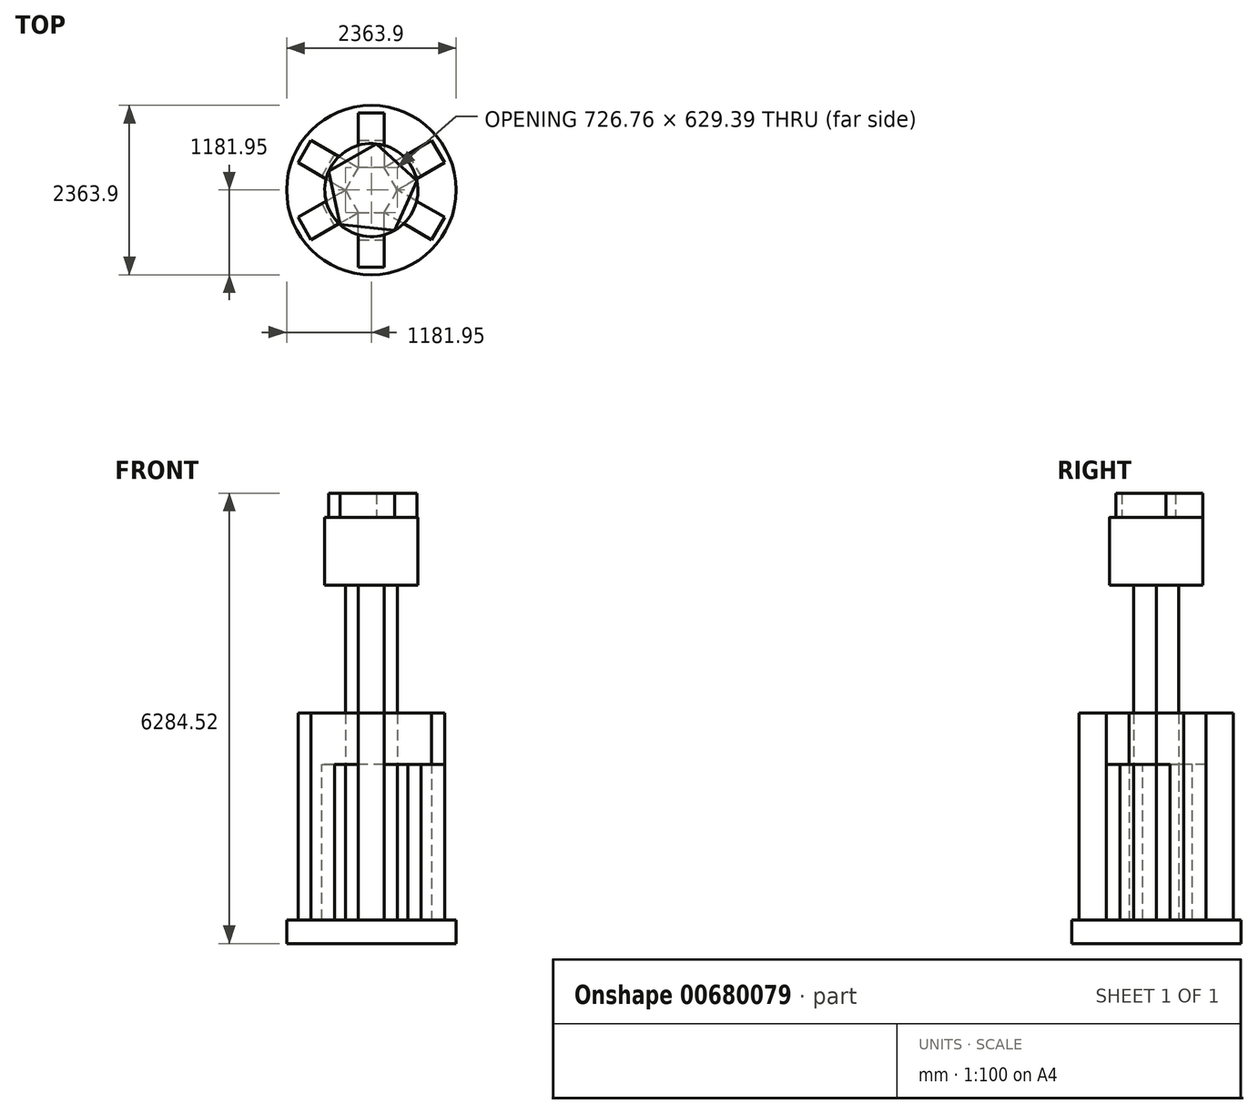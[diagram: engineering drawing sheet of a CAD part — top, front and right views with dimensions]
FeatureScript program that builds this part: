
annotation { "Feature Type Name" : "Feature", "Feature Type Description" : "" }
export const myFeature = defineFeature(function(context is Context, id is Id, definition is map)
    precondition{}
    {
        {
            var Q0;
            Q0=qCreatedBy(makeId("Top.planeOp"),FACE);
            var sketch = newSketch(context, id + "F0", { "sketchPlane" : qUnion([Q0])});
            skCircle(sketch, "E0.cCircle", {"center": v(0, 0) * mm, "radius": 363.38 * mm, "construction": true});
            skLineSegment(sketch, "E0.0", {"start": v(363.38, 0) * mm, "end": v(181.69, -314.7) * mm});
            skLineSegment(sketch, "E0.1", {"start": v(181.69, -314.7) * mm, "end": v(-181.69, -314.7) * mm});
            skLineSegment(sketch, "E0.2", {"start": v(-181.69, -314.7) * mm, "end": v(-363.38, 0) * mm});
            skLineSegment(sketch, "E0.3", {"start": v(-363.38, 0) * mm, "end": v(-181.69, 314.7) * mm});
            skLineSegment(sketch, "E0.4", {"start": v(-181.69, 314.7) * mm, "end": v(181.69, 314.7) * mm});
            skLineSegment(sketch, "E0.5", {"start": v(181.69, 314.7) * mm, "end": v(363.38, 0) * mm});
            skSolve(sketch);
        }
        {
            var Q0;
            Q0=makeQuery(id+"F0.imprint","IMPRINT",FACE,{"disambiguationData":[TD([[makeQuery(id+"F0.imprint","IMPRINT",EDGE,{"derivedFrom":sQuery(id+"F0.wireOp",EDGE,"E0.0")}),-1.0]])]});
            extrude(context, id + "F1", {"entities" : qUnion([Q0]), "depth" : 5000 * mm, "offsetDistance" : 25.4 * mm});
        }
        {
            var Q0;
            Q0=makeQuery(id+"F1.opExtrude","CAP_FACE",FACE,{"disambiguationData":[OSD([sQuery(id+"F0.wireOp",EDGE,"E0.0"),sQuery(id+"F0.wireOp",EDGE,"E0.1"),sQuery(id+"F0.wireOp",EDGE,"E0.2"),sQuery(id+"F0.wireOp",EDGE,"E0.3"),sQuery(id+"F0.wireOp",EDGE,"E0.4"),sQuery(id+"F0.wireOp",EDGE,"E0.5")])],"isStart":false});
            var sketch = newSketch(context, id + "F2", { "sketchPlane" : qUnion([Q0])});
            skCircle(sketch, "E1", {"center": v(0, 0) * mm, "radius": 650.1 * mm});
            skSolve(sketch);
        }
        {
            var Q0;
            Q0 = qSketchRegion(id + "F2", true);
            extrude(context, id + "F3", {"entities" : qUnion([Q0]), "operationType" : NewBodyOperationType.ADD, "depth" : 199.2 * mm, "offsetDistance" : 25.4 * mm});
        }
        {
            var Q0;
            Q0=makeQuery(id+"F1.opExtrude","SWEPT_FACE",FACE,{"disambiguationData":[OSD([sQuery(id+"F0.wireOp",EDGE,"E0.0")])]});
            var sketch = newSketch(context, id + "F4", { "sketchPlane" : qUnion([Q0])});
            skLineSegment(sketch, "E2.bottom", {"start": v(181.69, 3215.1) * mm, "end": v(-181.69, 3215.1) * mm});
            skLineSegment(sketch, "E2.top", {"start": v(181.69, 2500) * mm, "end": v(-181.69, 2500) * mm});
            skLineSegment(sketch, "E2.left", {"start": v(181.69, 3215.1) * mm, "end": v(181.69, 2500) * mm});
            skLineSegment(sketch, "E2.right", {"start": v(-181.69, 3215.1) * mm, "end": v(-181.69, 2500) * mm});
            skSolve(sketch);
        }
        {
            var Q0;
            Q0 = qSketchRegion(id + "F4", true);
            extrude(context, id + "F5", {"entities" : qUnion([Q0]), "operationType" : NewBodyOperationType.ADD, "depth" : 762 * mm, "offsetDistance" : 25.4 * mm});
        }
        {
            var Q0;
            Q0=makeQuery(id+"F1.opExtrude","SWEPT_FACE",FACE,{"disambiguationData":[OSD([sQuery(id+"F0.wireOp",EDGE,"E0.5")])]});
            var sketch = newSketch(context, id + "F6", { "sketchPlane" : qUnion([Q0])});
            skLineSegment(sketch, "E3.bottom", {"start": v(-181.69, 3215.1) * mm, "end": v(181.69, 3215.1) * mm});
            skLineSegment(sketch, "E3.top", {"start": v(-181.69, 2500) * mm, "end": v(181.69, 2500) * mm});
            skLineSegment(sketch, "E3.left", {"start": v(-181.69, 3215.1) * mm, "end": v(-181.69, 2500) * mm});
            skLineSegment(sketch, "E3.right", {"start": v(181.69, 3215.1) * mm, "end": v(181.69, 2500) * mm});
            skSolve(sketch);
        }
        {
            var Q0;
            Q0=makeQuery(id+"F6.imprint","IMPRINT",FACE,{"disambiguationData":[TD([[makeQuery(id+"F6.imprint","IMPRINT",EDGE,{"derivedFrom":sQuery(id+"F6.wireOp",EDGE,"E3.bottom")}),-1.0]])]});
            extrude(context, id + "F7", {"entities" : qUnion([Q0]), "operationType" : NewBodyOperationType.ADD, "depth" : 762 * mm, "offsetDistance" : 25.4 * mm});
        }
        {
            var Q0;
            Q0=makeQuery(id+"F1.opExtrude","SWEPT_FACE",FACE,{"disambiguationData":[OSD([sQuery(id+"F0.wireOp",EDGE,"E0.4")])]});
            var sketch = newSketch(context, id + "F8", { "sketchPlane" : qUnion([Q0])});
            skLineSegment(sketch, "E4.bottom", {"start": v(-181.69, 3215.1) * mm, "end": v(181.69, 3215.1) * mm});
            skLineSegment(sketch, "E4.top", {"start": v(-181.69, 2500) * mm, "end": v(181.69, 2500) * mm});
            skLineSegment(sketch, "E4.left", {"start": v(-181.69, 3215.1) * mm, "end": v(-181.69, 2500) * mm});
            skLineSegment(sketch, "E4.right", {"start": v(181.69, 3215.1) * mm, "end": v(181.69, 2500) * mm});
            skSolve(sketch);
        }
        {
            var Q0;
            Q0 = qSketchRegion(id + "F8", true);
            extrude(context, id + "F9", {"entities" : qUnion([Q0]), "operationType" : NewBodyOperationType.ADD, "depth" : 762 * mm, "offsetDistance" : 25.4 * mm});
        }
        {
            var Q0;
            Q0=makeQuery(id+"F1.opExtrude","SWEPT_FACE",FACE,{"disambiguationData":[OSD([sQuery(id+"F0.wireOp",EDGE,"E0.3")])]});
            var sketch = newSketch(context, id + "F10", { "sketchPlane" : qUnion([Q0])});
            skLineSegment(sketch, "E5.bottom", {"start": v(-181.69, 3215.1) * mm, "end": v(181.69, 3215.1) * mm});
            skLineSegment(sketch, "E5.top", {"start": v(-181.69, 2500) * mm, "end": v(181.69, 2500) * mm});
            skLineSegment(sketch, "E5.left", {"start": v(-181.69, 3215.1) * mm, "end": v(-181.69, 2500) * mm});
            skLineSegment(sketch, "E5.right", {"start": v(181.69, 3215.1) * mm, "end": v(181.69, 2500) * mm});
            skSolve(sketch);
        }
        {
            var Q0;
            Q0 = qSketchRegion(id + "F10", true);
            extrude(context, id + "F11", {"entities" : qUnion([Q0]), "operationType" : NewBodyOperationType.ADD, "depth" : 762 * mm, "offsetDistance" : 25.4 * mm});
        }
        {
            var Q0;
            Q0=makeQuery(id+"F1.opExtrude","SWEPT_FACE",FACE,{"disambiguationData":[OSD([sQuery(id+"F0.wireOp",EDGE,"E0.1")])]});
            var sketch = newSketch(context, id + "F12", { "sketchPlane" : qUnion([Q0])});
            skLineSegment(sketch, "E6.bottom", {"start": v(181.69, 3215.1) * mm, "end": v(-181.69, 3215.1) * mm});
            skLineSegment(sketch, "E6.top", {"start": v(181.69, 2500) * mm, "end": v(-181.69, 2500) * mm});
            skLineSegment(sketch, "E6.left", {"start": v(181.69, 3215.1) * mm, "end": v(181.69, 2500) * mm});
            skLineSegment(sketch, "E6.right", {"start": v(-181.69, 3215.1) * mm, "end": v(-181.69, 2500) * mm});
            skSolve(sketch);
        }
        {
            var Q0;
            Q0=makeQuery(id+"F12.imprint","IMPRINT",FACE,{"disambiguationData":[TD([[makeQuery(id+"F12.imprint","IMPRINT",EDGE,{"derivedFrom":sQuery(id+"F12.wireOp",EDGE,"E6.bottom")}),1.0]])]});
            extrude(context, id + "F13", {"entities" : qUnion([Q0]), "operationType" : NewBodyOperationType.ADD, "depth" : 762 * mm, "offsetDistance" : 25.4 * mm});
        }
        {
            var Q0;
            Q0=makeQuery(id+"F1.opExtrude","SWEPT_FACE",FACE,{"disambiguationData":[OSD([sQuery(id+"F0.wireOp",EDGE,"E0.2")])]});
            var sketch = newSketch(context, id + "F14", { "sketchPlane" : qUnion([Q0])});
            skLineSegment(sketch, "E7.bottom", {"start": v(-181.69, 3215.1) * mm, "end": v(181.69, 3215.1) * mm});
            skLineSegment(sketch, "E7.top", {"start": v(-181.69, 2500) * mm, "end": v(181.69, 2500) * mm});
            skLineSegment(sketch, "E7.left", {"start": v(-181.69, 3215.1) * mm, "end": v(-181.69, 2500) * mm});
            skLineSegment(sketch, "E7.right", {"start": v(181.69, 3215.1) * mm, "end": v(181.69, 2500) * mm});
            skSolve(sketch);
        }
        {
            var Q0;
            Q0=makeQuery(id+"F14.imprint","IMPRINT",FACE,{"disambiguationData":[TD([[makeQuery(id+"F14.imprint","IMPRINT",EDGE,{"derivedFrom":sQuery(id+"F14.wireOp",EDGE,"E7.bottom")}),-1.0]])]});
            extrude(context, id + "F15", {"entities" : qUnion([Q0]), "operationType" : NewBodyOperationType.ADD, "depth" : 762 * mm, "offsetDistance" : 25.4 * mm});
        }
        {
            var Q0;
            Q0=makeQuery(id+"F1.opExtrude","CAP_FACE",FACE,{"disambiguationData":[OSD([sQuery(id+"F0.wireOp",EDGE,"E0.0"),sQuery(id+"F0.wireOp",EDGE,"E0.1"),sQuery(id+"F0.wireOp",EDGE,"E0.2"),sQuery(id+"F0.wireOp",EDGE,"E0.3"),sQuery(id+"F0.wireOp",EDGE,"E0.4"),sQuery(id+"F0.wireOp",EDGE,"E0.5")])],"isStart":true});
            var sketch = newSketch(context, id + "F16", { "sketchPlane" : qUnion([Q0])});
            skCircle(sketch, "E8", {"center": v(0, 0) * mm, "radius": 1181.95 * mm});
            skSolve(sketch);
        }
        {
            var Q0;
            Q0 = qSketchRegion(id + "F16", true);
            extrude(context, id + "F17", {"entities" : qUnion([Q0]), "operationType" : NewBodyOperationType.ADD, "oppositeDirection" : true, "depth" : 326.88 * mm, "offsetDistance" : 25.4 * mm});
        }
        {
            var Q0;
            Q0=makeQuery(id+"F9.opExtrude","SWEPT_FACE",FACE,{"disambiguationData":[OSD([sQuery(id+"F8.wireOp",EDGE,"E4.top")])]});
            var sketch = newSketch(context, id + "F18", { "sketchPlane" : qUnion([Q0])});
            skLineSegment(sketch, "E9", {"start": v(181.69, -695.7) * mm, "end": v(-181.69, -695.7) * mm});
            skSolve(sketch);
        }
        {
            var Q0;
            {var subQ0=sQuery(id+"F18.wireOp",EDGE,"E9");Q0=makeQuery(id+"F18.imprint","IMPRINT",FACE,{"disambiguationData":[TD([[makeQuery(id+"F18.imprint","IMPRINT",EDGE,{"derivedFrom":subQ0}),1.0]])]});}
            extrude(context, id + "F19", {"entities" : qUnion([Q0]), "operationType" : NewBodyOperationType.ADD, "depth" : 1809.93 * mm, "offsetDistance" : 25.4 * mm});
        }
        {
            var Q0;
            Q0=makeQuery(id+"F7.opExtrude","SWEPT_FACE",FACE,{"disambiguationData":[OSD([sQuery(id+"F6.wireOp",EDGE,"E3.top")])]});
            var sketch = newSketch(context, id + "F20", { "sketchPlane" : qUnion([Q0])});
            skLineSegment(sketch, "E10", {"start": v(693.34, -190.5) * mm, "end": v(511.65, -505.2) * mm});
            skSolve(sketch);
        }
        {
            var Q0;
            Q0=makeQuery(id+"F5.opExtrude","SWEPT_FACE",FACE,{"disambiguationData":[OSD([sQuery(id+"F4.wireOp",EDGE,"E2.top")])]});
            var sketch = newSketch(context, id + "F21", { "sketchPlane" : qUnion([Q0])});
            skLineSegment(sketch, "E11", {"start": v(511.65, 505.2) * mm, "end": v(693.34, 190.5) * mm});
            skLineSegment(sketch, "E12", {"start": v(693.34, 190.5) * mm, "end": v(511.65, 505.2) * mm});
            skSolve(sketch);
        }
        {
            var Q0;
            Q0=makeQuery(id+"F13.opExtrude","SWEPT_FACE",FACE,{"disambiguationData":[OSD([sQuery(id+"F12.wireOp",EDGE,"E6.top")])]});
            var sketch = newSketch(context, id + "F22", { "sketchPlane" : qUnion([Q0])});
            skLineSegment(sketch, "E13", {"start": v(181.69, 695.7) * mm, "end": v(-181.69, 695.7) * mm});
            skSolve(sketch);
        }
        {
            var Q0;
            Q0=makeQuery(id+"F15.opExtrude","SWEPT_FACE",FACE,{"disambiguationData":[OSD([sQuery(id+"F14.wireOp",EDGE,"E7.top")])]});
            var sketch = newSketch(context, id + "F23", { "sketchPlane" : qUnion([Q0])});
            skLineSegment(sketch, "E14", {"start": v(-511.65, 505.2) * mm, "end": v(-693.34, 190.5) * mm});
            skSolve(sketch);
        }
        {
            var Q0;
            {var subQ0=sQuery(id+"F20.wireOp",EDGE,"E10");Q0=makeQuery(id+"F20.imprint","IMPRINT",FACE,{"disambiguationData":[TD([[makeQuery(id+"F20.imprint","IMPRINT",EDGE,{"derivedFrom":subQ0}),1.0]])]});}
            var Q1;
            {var subQ0=sQuery(id+"F23.wireOp",EDGE,"E14");Q1=makeQuery(id+"F23.imprint","IMPRINT",FACE,{"disambiguationData":[TD([[makeQuery(id+"F23.imprint","IMPRINT",EDGE,{"derivedFrom":subQ0}),-1.0]])]});}
            var Q2;
            {var subQ0=sQuery(id+"F22.wireOp",EDGE,"E13");Q2=makeQuery(id+"F22.imprint","IMPRINT",FACE,{"disambiguationData":[TD([[makeQuery(id+"F22.imprint","IMPRINT",EDGE,{"derivedFrom":subQ0}),-1.0]])]});}
            var Q3;
            {var subQ0=sQuery(id+"F21.wireOp",EDGE,"E12");Q3=makeQuery(id+"F21.imprint","IMPRINT",FACE,{"disambiguationData":[TD([[makeQuery(id+"F21.imprint","IMPRINT",EDGE,{"derivedFrom":subQ0}),-1.0]])]});}
            extrude(context, id + "F24", {"entities" : qUnion([Q0, Q1, Q2, Q3]), "operationType" : NewBodyOperationType.ADD, "depth" : 2253.76 * mm, "offsetDistance" : 25.4 * mm});
        }
        {
            var Q0;
            Q0=makeQuery(id+"F19.opExtrude","CAP_FACE",FACE,{"disambiguationData":[OSD([sQuery(id+"F0.wireOp",EDGE,"E0.3"),sQuery(id+"F0.wireOp",EDGE,"E0.4"),sQuery(id+"F0.wireOp",EDGE,"E0.5"),sQuery(id+"F8.wireOp",EDGE,"E4.top"),sQuery(id+"F8.wireOp",EDGE,"E4.left"),sQuery(id+"F8.wireOp",EDGE,"E4.right"),sQuery(id+"F18.wireOp",EDGE,"E9")])],"isStart":false});
            extrude(context, id + "F25", {"entities" : qUnion([Q0]), "operationType" : NewBodyOperationType.ADD, "depth" : 666.82 * mm, "offsetDistance" : 25.4 * mm});
        }
        {
            var Q0;
            Q0=makeQuery(id+"F11.opExtrude","SWEPT_FACE",FACE,{"disambiguationData":[OSD([sQuery(id+"F10.wireOp",EDGE,"E5.top")])]});
            var sketch = newSketch(context, id + "F26", { "sketchPlane" : qUnion([Q0])});
            skLineSegment(sketch, "E15", {"start": v(-511.65, -505.2) * mm, "end": v(-693.34, -190.5) * mm});
            skSolve(sketch);
        }
        {
            var Q0;
            {var subQ0=sQuery(id+"F26.wireOp",EDGE,"E15");Q0=makeQuery(id+"F26.imprint","IMPRINT",FACE,{"disambiguationData":[TD([[makeQuery(id+"F26.imprint","IMPRINT",EDGE,{"derivedFrom":subQ0}),1.0]])]});}
            extrude(context, id + "F27", {"entities" : qUnion([Q0]), "operationType" : NewBodyOperationType.ADD, "depth" : 2417.54 * mm, "offsetDistance" : 25.4 * mm});
        }
        {
            var Q0;
            Q0=makeQuery(id+"F3.opExtrude","CAP_FACE",FACE,{"disambiguationData":[OSD([sQuery(id+"F2.wireOp",EDGE,"E1")])],"isStart":false});
            extrude(context, id + "F28", {"entities" : qUnion([Q0]), "operationType" : NewBodyOperationType.ADD, "depth" : 751.47 * mm, "offsetDistance" : 25.4 * mm});
        }
        {
            var Q0;
            Q0=makeQuery(id+"F28.opExtrude","CAP_FACE",FACE,{"disambiguationData":[OSD([sQuery(id+"F2.wireOp",EDGE,"E1")])],"isStart":false});
            var sketch = newSketch(context, id + "F29", { "sketchPlane" : qUnion([Q0])});
            skCircle(sketch, "E16.cCircle", {"center": v(0, 0) * mm, "radius": 650.1 * mm, "construction": true});
            skLineSegment(sketch, "E16.0", {"start": v(-593.07, 266.28) * mm, "end": v(69.98, 646.33) * mm});
            skLineSegment(sketch, "E16.1", {"start": v(69.98, 646.33) * mm, "end": v(636.32, 133.17) * mm});
            skLineSegment(sketch, "E16.2", {"start": v(636.32, 133.17) * mm, "end": v(323.28, -564.03) * mm});
            skLineSegment(sketch, "E16.3", {"start": v(323.28, -564.03) * mm, "end": v(-436.52, -481.76) * mm});
            skLineSegment(sketch, "E16.4", {"start": v(-436.52, -481.76) * mm, "end": v(-593.07, 266.28) * mm});
            skSolve(sketch);
        }
        {
            var Q0;
            Q0=makeQuery(id+"F29.imprint","IMPRINT",FACE,{"disambiguationData":[TD([[makeQuery(id+"F29.imprint","IMPRINT",EDGE,{"derivedFrom":sQuery(id+"F29.wireOp",EDGE,"E16.0")}),-1.0]])]});
            extrude(context, id + "F30", {"entities" : qUnion([Q0]), "operationType" : NewBodyOperationType.ADD, "depth" : 333.85 * mm, "offsetDistance" : 25.4 * mm});
        }
    });
